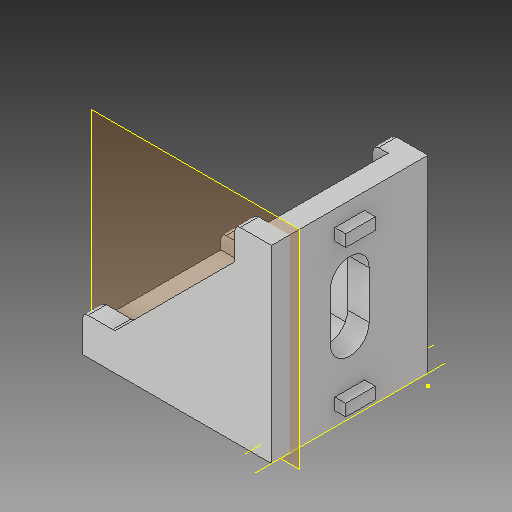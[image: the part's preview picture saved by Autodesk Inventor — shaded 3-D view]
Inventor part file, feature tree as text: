
AUTODESK INVENTOR PART (.ipt)
format: ipt  version: 2017 (Build 210142000, 142)  size: 220,160 bytes
history: native  units: mm
features: sketch x8, extrude x5, other x2, plane x1, fillet x1, pattern_circular x1, projected_geometry x1
ambient origin geometry x8: Origin, YZ Plane, XZ Plane, XY Plane, X Axis, Y Axis, Z Axis, Center Point
bodies: Solid1 (feature_tree)
feature tree (19):
  extrude  "Extrusion1"  Depth=6.8mm
  plane  "Work Plane1"
  extrude  "Extrusion2"  Depth=6.0mm
  extrude  "Extrusion3"  TaperAngle=180.0deg  [1 undecoded]
  fillet  "Fillet1"  Radius=6.8mm
  sketch  "Sketch4"  dims[d7=6.0mm]
  other  "Work Axis1"
  pattern_circular  "Circular Pattern1"  [2 undecoded]
  extrude  "Extrusion4"  Depth=22.2mm TaperAngle=0.0deg
  other  "Work Axis2"
  sketch  "Sketch7"  dims[d9=1.0mm]
  extrude  "Extrusion5"  Depth=2.0mm
  sketch  "Sketch10"  dims[d12=-3.4mm d13=4.0mm d14=22.2mm d15=0.0mm d16=9.0mm d17=3.6mm d18=16.0mm d19=3.6mm d20=22.2mm d21=0.0mm d22=1.0mm d23=2.0mm d24=2.0mm d25=2.0mm d26=20.0mm d27=270.0deg d29=3.0mm d30=0.0mm d31=2.75mm d32=5.5mm d33=2.2mm d34=2.6mm d35=2.75mm d36=2.2mm d37=5.5mm d38=2.0mm d39=0.0mm d41=2.0mm d42=0.0mm]
  sketch  "Sketch1"  dims[d0=35.0mm d1=6.8mm]
  sketch  "Sketch2"  dims[d2=90.0deg d3=6.0mm]
  sketch  "Sketch3"  dims[d4=35.0mm d5=180.0deg d6=6.8mm]
  sketch  "Sketch5"  dims[d8=90.0deg]
  sketch  "Sketch9"  dims[d10=29.0mm d11=0.0mm]
  projected_geometry  "Projected Loop4"
note: 3 required parameter values undecoded (feature->parameter linkage not recoverable at this tier; creation-order binding heuristic only, values carry confidence <= 0.55)
